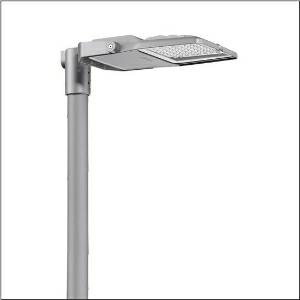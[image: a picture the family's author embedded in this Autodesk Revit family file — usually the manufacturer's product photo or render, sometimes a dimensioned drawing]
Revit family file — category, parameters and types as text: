
# Revit family: floodlight_fl_21_iq_mini___pl43_5xa7772b4a3a_1e53
name_source: partatom
category: Lighting Fixtures
units: mm (PartAtom-declared; Revit-internal decimal feet)

## family parameters
Cut with Voids When Loaded = No
Host = Face
Light Source = No
Part Type = Normal
Room Calculation Point = No
Round Connector Dimension = Use Diameter
Shared = No

## types (1)
- --- (1 x LED, 6660 lm, 45.5 W, 4000K)
    Apparent Load = 46 VA
    CIE Flux Codes = 27 78 99 100 100
    Color Rendering = 70
    Color Temperature = 4000K
    Default Elevation = 1800 mm
    Description = Floodlight FL 21 iQ mini, floodlight, primary light control with lens, of PMMA, primary optical cover: protective disc, of toughened safety glass, transparent, light distribution: PL43, light emission: direct distribution, installation type: surface-mounted, lamps: LED, High Power LED, rated values: 6.660lm | 45,5W | 146,4lm/W (begin service life); end service life: 6.660lm | 48W; at 50% lumin. flux: 3.330lm | 21,5W | 154,9lm/W, colour temperature: 4000K, colour rendering: CRI > 70, light colour: 740, light setting 1 begin service life: 100% | 6.660lm | 45,5W | 146,4lm/W | 4.000K, light setting 1 end service life: 48W, further light settings possible, control: pre-setting: linear dimming characteristic, Auto-Match, Temp-Guard, Night-Set, Smart-Wire, Desk-Remote (wireless, voltage-free reading and setting of iQ features in the workshop via application-optimized NFC function/RFID function), optimised constant luminous flux control (CLO 2.0), Light-Fading, Lumen-Switch, with terminal, 6-pole, mains connection: 220..240V, AC, 50/60Hz, luminaire housing, of diecast aluminium, powder-coated, SITECO metallic grey (DB 702S), corrosivity category C5 mid according to DIN EN ISO 12944suitable for swimming poolschlorine-resistant, sealing non-destructively replaceable, please order mast flange separately, mast bracket, of steel, galvanised, powder-coated, protection rating (complete): IP66, insulation class (complete): insulation class II (safety insulation), certification: CE, ENEC, VDE, protection symbol: D, impact resistance: IK08, permissible operating ambient temperature: -40..+40°C, permissible operating ambient temperature for outdoor applications: -40..+50°C, standard: DIN EN 12944, LABS conformity tested according to VDMA 24364:2018-05, packaging unit: 1 piece

Light Distribution: PL43
    Height = 70 mm
    Lamp = 1 x LED
    Lamp Light Flux = 6660 lm
    Lamp Power = 45.5 W
    Lamp count = 1
    Length = 485 mm
    Luminous efficacy = 146 lm/W
    Manufacturer = Siteco
    ModVariant = No
    Model = 5XA7772B4A3A
    Number of Poles = 1
    OnlyDefault = Yes
    Power Factor = 1
    Product Name = Floodlight FL 21 iQ mini | PL43
    Product group = floodlight | pylon annexe
    ProductGroupID = 6201
    Protection Class = Protection class II
    Protection Degree = IP 66
    RLX_Detail_Level = 1
    RLX_Emergency_Light_Flux = 0 lm
    RLX_Emergency_Type = 0
    RLX_Emergency_Type_DB = No
    RlxData = <blob elided: 101449 chars, md5=ef7da2cc>
    Socket = socket
    Standby Power = 0 W
    System Light Flux = 6660 lm
    System Power = 46 W
    Type Comments = factory setting: luminous flux: 100 % | dim-lin: 254 | 463 mA
    Type Image = l_1007125.jpg
    URL = http://relux.com
    VarID = @adj_162143
    Voltage = 0 V
    Weight = 0.00 kg
    Width = 337 mm

## geometry (parser evidence)
native form markers: Blend x4, Sweep x12
no freeform markers — native parametric forms only
